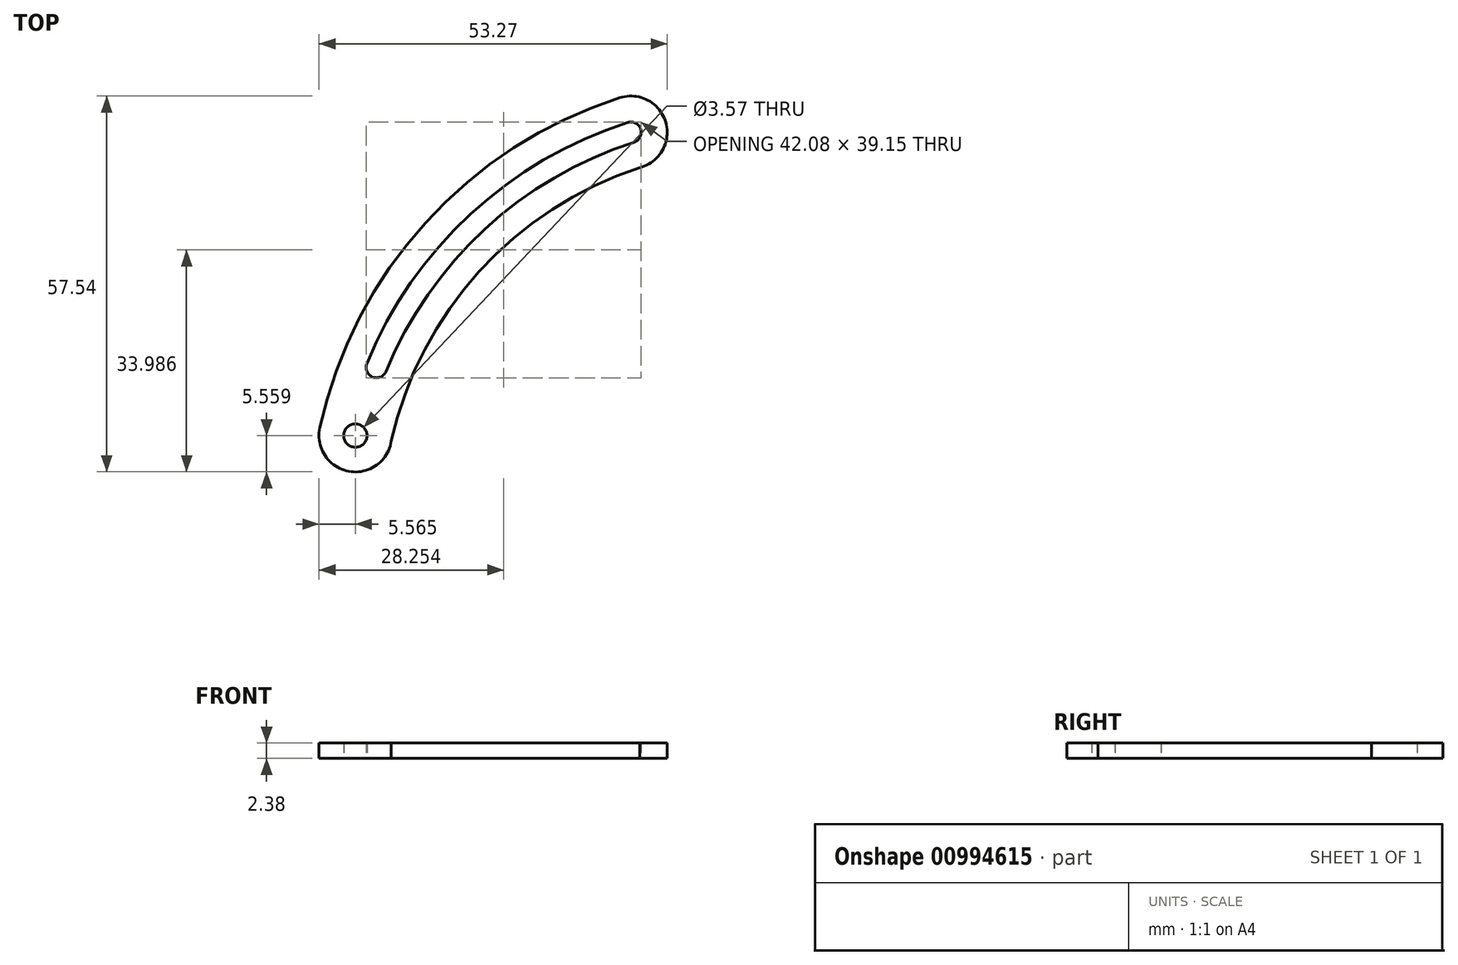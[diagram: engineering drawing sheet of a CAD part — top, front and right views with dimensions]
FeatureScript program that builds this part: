
annotation { "Feature Type Name" : "Feature", "Feature Type Description" : "" }
export const myFeature = defineFeature(function(context is Context, id is Id, definition is map)
    precondition{}
    {
        {
            var Q0;
            Q0=qCreatedBy(makeId("Top.planeOp"),FACE);
            var sketch = newSketch(context, id + "F0", { "sketchPlane" : qUnion([Q0])});
            skArc(sketch, "E0", {"start": v(-17.78, 54.31) * mm, "mid": v(-42.31, 38.42) * mm, "end": v(-55.77, 12.46) * mm});
            skArc(sketch, "E1", {"start": v(-20.83, 65) * mm, "mid": v(-50.54, 45.89) * mm, "end": v(-66.71, 14.47) * mm});
            skPoint(sketch, "E2", {"position": v(-19.13, 59.71) * mm});
            skPoint(sketch, "E3", {"position": v(-61.28, 13.29) * mm});
            skArc(sketch, "E4.trimOffspring", {"start": v(-17.78, 54.31) * mm, "mid": v(-13.78, 61.24) * mm, "end": v(-20.83, 65) * mm});
            skArc(sketch, "E5.trimOffspring", {"start": v(-66.71, 14.47) * mm, "mid": v(-62.28, 7.82) * mm, "end": v(-55.77, 12.46) * mm});
            skPoint(sketch, "E6", {"position": v(-58.04, 23.73) * mm});
            skArc(sketch, "E7.0.startCap", {"start": v(-56.57, 23.13) * mm, "mid": v(-58.64, 22.26) * mm, "end": v(-59.5, 24.33) * mm});
            skArc(sketch, "E7.0.endCap", {"start": v(-19.61, 61.22) * mm, "mid": v(-17.62, 60.2) * mm, "end": v(-18.65, 58.2) * mm});
            skArc(sketch, "E7.0.left", {"start": v(-59.5, 24.33) * mm, "mid": v(-43.65, 47.2) * mm, "end": v(-19.61, 61.22) * mm});
            skArc(sketch, "E7.0.right", {"start": v(-56.57, 23.13) * mm, "mid": v(-41.5, 44.87) * mm, "end": v(-18.65, 58.2) * mm});
            skCircle(sketch, "E8", {"center": v(-61.28, 13.29) * mm, "radius": 1.79 * mm});
            skSolve(sketch);
        }
        {
            var Q0;
            Q0=makeQuery(id+"F0.imprint","IMPRINT",FACE,{"disambiguationData":[TD([[makeQuery(id+"F0.imprint","IMPRINT",EDGE,{"derivedFrom":sQuery(id+"F0.wireOp",EDGE,"E0")}),-1.0]])]});
            extrude(context, id + "F1", {"entities" : qUnion([Q0]), "depth" : 2.38 * mm, "offsetDistance" : 25.4 * mm});
        }
    });
